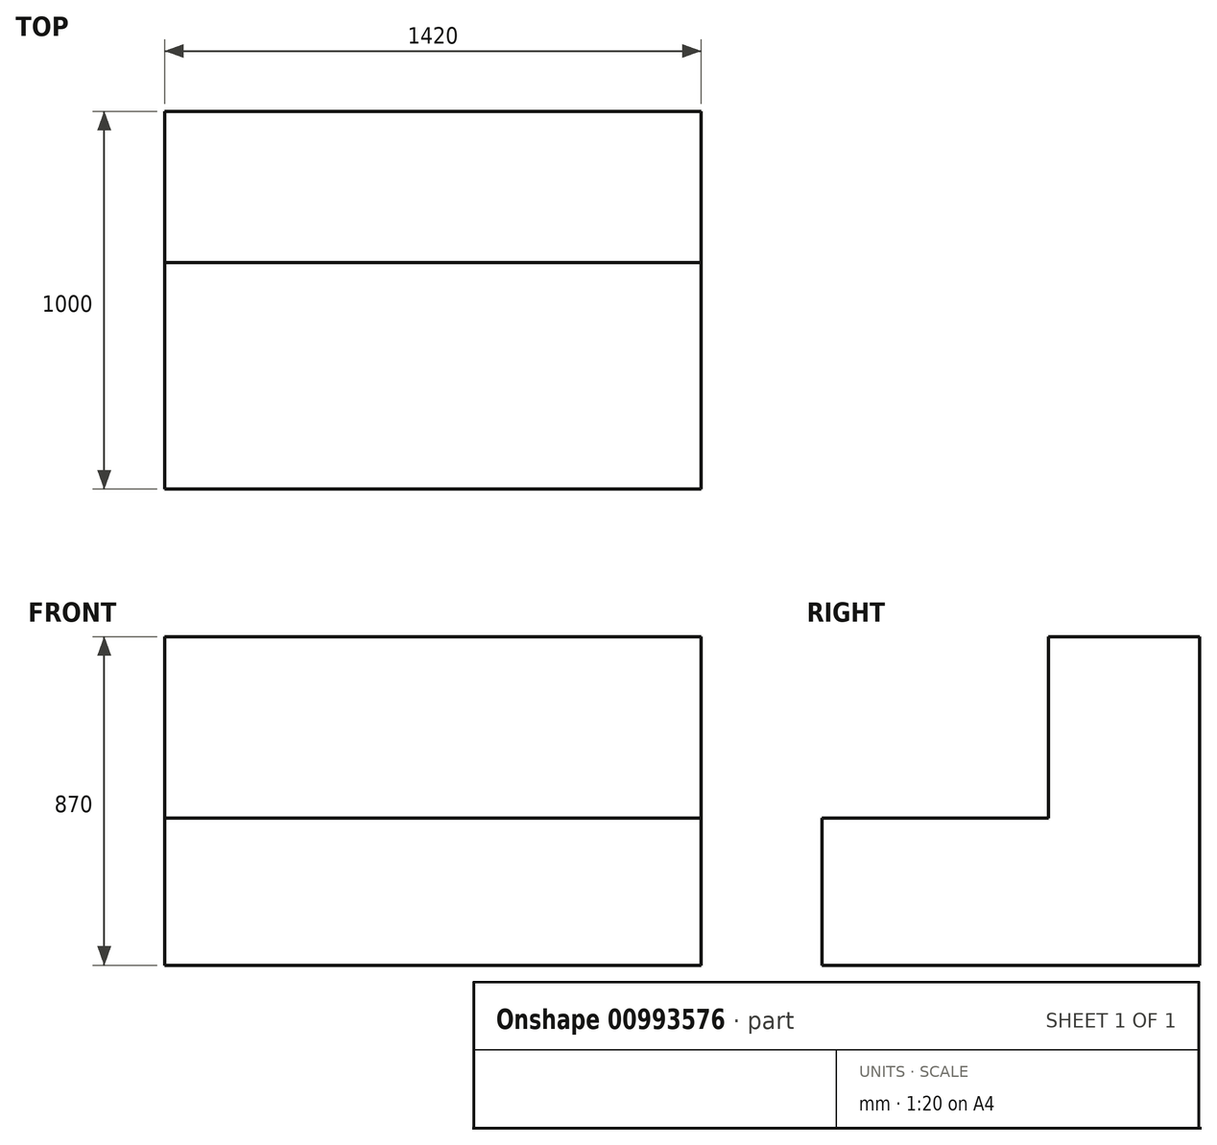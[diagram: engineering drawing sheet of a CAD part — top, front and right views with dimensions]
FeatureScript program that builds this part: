
annotation { "Feature Type Name" : "Feature", "Feature Type Description" : "" }
export const myFeature = defineFeature(function(context is Context, id is Id, definition is map)
    precondition{}
    {
        {
            var Q0;
            Q0=qCreatedBy(makeId("Right.planeOp"),FACE);
            var sketch = newSketch(context, id + "F0", { "sketchPlane" : qUnion([Q0])});
            skLineSegment(sketch, "E0", {"start": v(0, 0) * mm, "end": v(0, 870) * mm});
            skLineSegment(sketch, "E1", {"start": v(0, 870) * mm, "end": v(-400, 870) * mm});
            skLineSegment(sketch, "E2", {"start": v(-400, 870) * mm, "end": v(-400, 390) * mm});
            skLineSegment(sketch, "E3", {"start": v(-400, 390) * mm, "end": v(-1000, 390) * mm});
            skLineSegment(sketch, "E4", {"start": v(-1000, 390) * mm, "end": v(-1000, 0) * mm});
            skLineSegment(sketch, "E5", {"start": v(-1000, 0) * mm, "end": v(0, 0) * mm});
            skSolve(sketch);
        }
        {
            var Q0;
            Q0=makeQuery(id+"F0.imprint","IMPRINT",FACE,{"disambiguationData":[TD([[makeQuery(id+"F0.imprint","IMPRINT",EDGE,{"derivedFrom":sQuery(id+"F0.wireOp",EDGE,"E0")}),1.0]])]});
            extrude(context, id + "F1", {"entities" : qUnion([Q0]), "endBound" : BoundingType.SYMMETRIC, "depth" : 1420 * mm, "offsetDistance" : 25 * mm});
        }
    });
